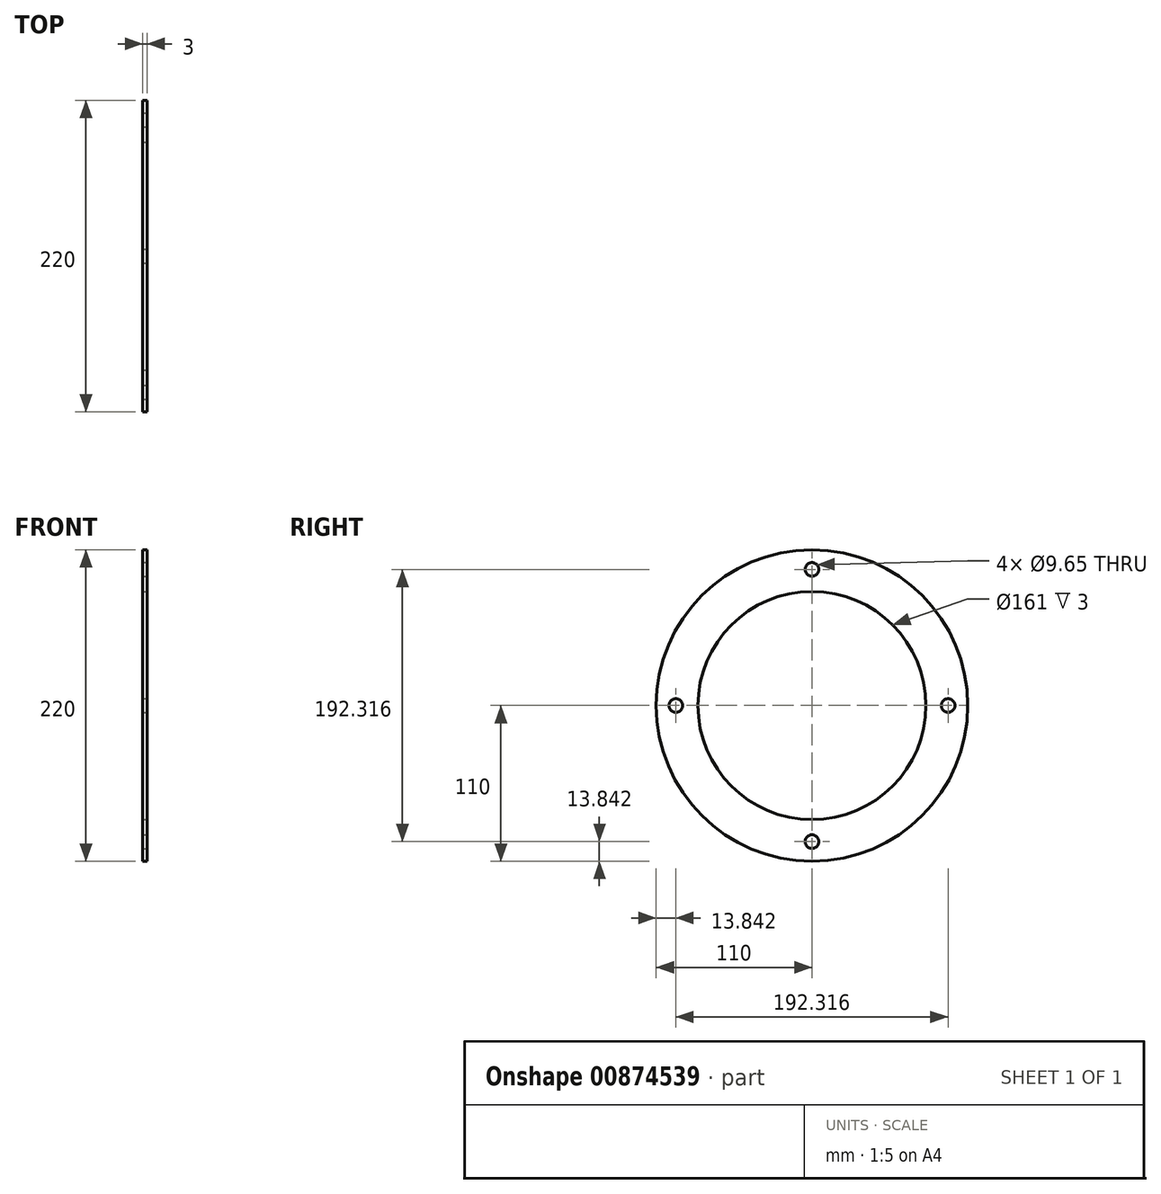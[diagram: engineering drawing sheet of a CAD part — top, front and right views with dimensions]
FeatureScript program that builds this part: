
annotation { "Feature Type Name" : "Feature", "Feature Type Description" : "" }
export const myFeature = defineFeature(function(context is Context, id is Id, definition is map)
    precondition{}
    {
        {
            var Q0;
            Q0=qCreatedBy(makeId("Right.planeOp"),FACE);
            var sketch = newSketch(context, id + "F0", { "sketchPlane" : qUnion([Q0])});
            skCircle(sketch, "E0", {"center": v(0, 0) * mm, "radius": 110 * mm});
            skCircle(sketch, "E1", {"center": v(0, 0) * mm, "radius": 80.5 * mm});
            skSolve(sketch);
        }
        {
            var Q0;
            Q0=makeQuery(id+"F0.imprint","IMPRINT",FACE,{"disambiguationData":[TD([[makeQuery(id+"F0.imprint","IMPRINT",EDGE,{"derivedFrom":sQuery(id+"F0.wireOp",EDGE,"E0")}),1.0]])]});
            extrude(context, id + "F1", {"entities" : qUnion([Q0]), "oppositeDirection" : true, "depth" : 3 * mm, "offsetDistance" : 25 * mm});
        }
        {
            var Q0;
            Q0=makeQuery(id+"F1.opExtrude","CAP_FACE",FACE,{"disambiguationData":[OSD([sQuery(id+"F0.wireOp",EDGE,"E0"),sQuery(id+"F0.wireOp",EDGE,"E1")])],"isStart":true});
            var sketch = newSketch(context, id + "F2", { "sketchPlane" : qUnion([Q0])});
            skCircle(sketch, "E2", {"center": v(0, 96.16) * mm, "radius": 4.83 * mm});
            skCircle(sketch, "E3.1.0", {"center": v(-96.16, 0) * mm, "radius": 4.83 * mm});
            skCircle(sketch, "E3.2.0", {"center": v(0, -96.16) * mm, "radius": 4.83 * mm});
            skCircle(sketch, "E3.3.0", {"center": v(96.16, 0) * mm, "radius": 4.83 * mm});
            skPoint(sketch, "E3.center", {"position": v(0, 0) * mm});
            skSolve(sketch);
        }
        {
            var Q0;
            Q0=makeQuery(id+"F2.imprint","IMPRINT",FACE,{"disambiguationData":[TD([[makeQuery(id+"F2.imprint","IMPRINT",EDGE,{"derivedFrom":sQuery(id+"F2.wireOp",EDGE,"E2")}),1.0]])]});
            var Q1;
            Q1=makeQuery(id+"F2.imprint","IMPRINT",FACE,{"disambiguationData":[TD([[makeQuery(id+"F2.imprint","IMPRINT",EDGE,{"derivedFrom":sQuery(id+"F2.wireOp",EDGE,"E3.1.0")}),1.0]])]});
            var Q2;
            Q2=makeQuery(id+"F2.imprint","IMPRINT",FACE,{"disambiguationData":[TD([[makeQuery(id+"F2.imprint","IMPRINT",EDGE,{"derivedFrom":sQuery(id+"F2.wireOp",EDGE,"E3.2.0")}),1.0]])]});
            var Q3;
            Q3=makeQuery(id+"F2.imprint","IMPRINT",FACE,{"disambiguationData":[TD([[makeQuery(id+"F2.imprint","IMPRINT",EDGE,{"derivedFrom":sQuery(id+"F2.wireOp",EDGE,"E3.3.0")}),1.0]])]});
            extrude(context, id + "F3", {"entities" : qUnion([Q0, Q1, Q2, Q3]), "operationType" : NewBodyOperationType.REMOVE, "oppositeDirection" : true, "depth" : 5 * mm, "offsetDistance" : 25 * mm});
        }
    });
